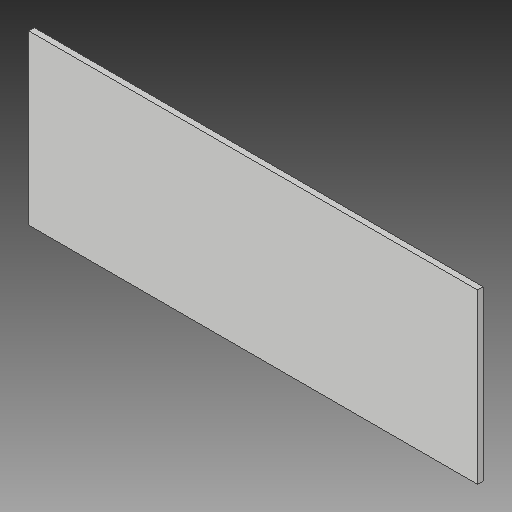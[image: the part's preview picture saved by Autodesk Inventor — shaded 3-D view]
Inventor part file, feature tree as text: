
AUTODESK INVENTOR PART (.ipt)
format: ipt  version: 2018 (Build 220112000, 112)  size: 79,872 bytes
history: native  units: in
note: dims shown in document units (in); Inventor stores cm internally (conversion verified against a paired STEP export)
features: other x3, sketch x1
ambient origin geometry x8: Origin, YZ Plane, XZ Plane, XY Plane, X Axis, Y Axis, Z Axis, Center Point
bodies: Solid1 (feature_tree)
feature tree (4):
  other  "solarpanel.ipt"
  other  "Solid1::solarpanel.ipt"
  other  "TaggingFeature1"
  sketch  "Sketch1"  dims[d0=0.3937in]
